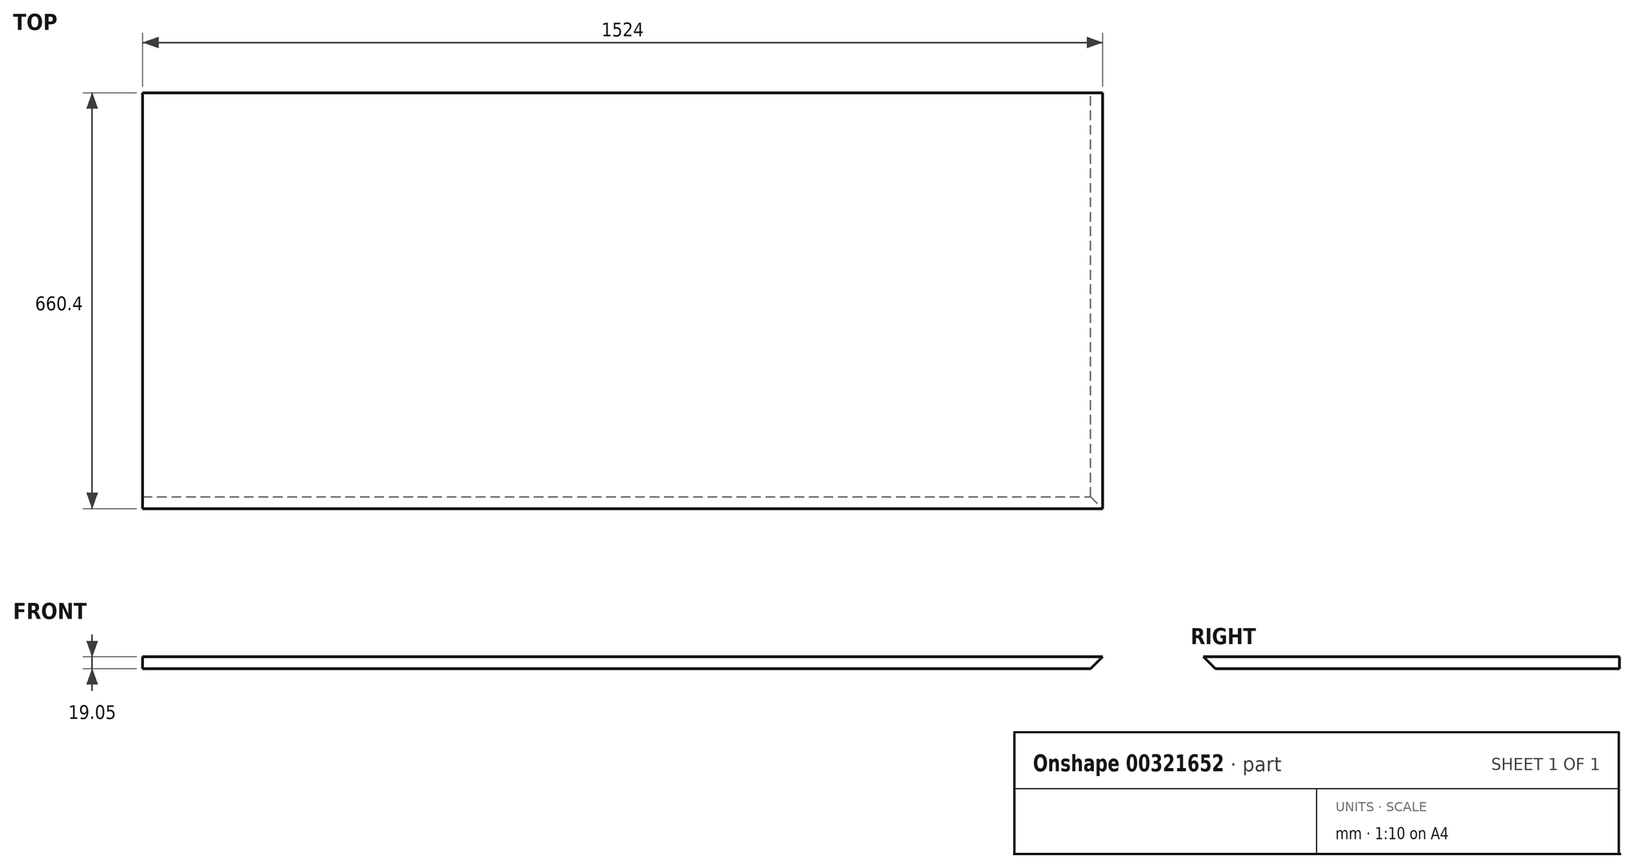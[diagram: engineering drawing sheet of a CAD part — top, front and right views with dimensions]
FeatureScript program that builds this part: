
annotation { "Feature Type Name" : "Feature", "Feature Type Description" : "" }
export const myFeature = defineFeature(function(context is Context, id is Id, definition is map)
    precondition{}
    {
        {
            var Q0;
            Q0=qCreatedBy(makeId("Top.planeOp"),FACE);
            var sketch = newSketch(context, id + "F0", { "sketchPlane" : qUnion([Q0])});
            skLineSegment(sketch, "E0.bottom", {"start": v(762, 330.2) * mm, "end": v(-762, 330.2) * mm});
            skLineSegment(sketch, "E0.top", {"start": v(762, -330.2) * mm, "end": v(-762, -330.2) * mm});
            skLineSegment(sketch, "E0.left", {"start": v(762, 330.2) * mm, "end": v(762, -330.2) * mm});
            skLineSegment(sketch, "E0.right", {"start": v(-762, 330.2) * mm, "end": v(-762, -330.2) * mm});
            skPoint(sketch, "E0.middle", {"position": v(0, 0) * mm});
            skSolve(sketch);
        }
        {
            var Q0;
            Q0=makeQuery(id+"F0.imprint","IMPRINT",FACE,{"disambiguationData":[TD([[makeQuery(id+"F0.imprint","IMPRINT",EDGE,{"derivedFrom":sQuery(id+"F0.wireOp",EDGE,"E0.bottom")}),1.0]])]});
            extrude(context, id + "F1", {"entities" : qUnion([Q0]), "depth" : 19.05 * mm});
        }
        {
            var Q0;
            Q0=makeQuery(id+"F1.opExtrude","SWEPT_FACE",FACE,{"disambiguationData":[OSD([sQuery(id+"F0.wireOp",EDGE,"E0.left")])]});
            var sketch = newSketch(context, id + "F2", { "sketchPlane" : qUnion([Q0])});
            skLineSegment(sketch, "E1", {"start": v(-330.2, 19.05) * mm, "end": v(-311.15, 0) * mm});
            skLineSegment(sketch, "E2", {"start": v(-311.15, 0) * mm, "end": v(-330.2, 0) * mm});
            skLineSegment(sketch, "E3", {"start": v(-330.2, 0) * mm, "end": v(-330.2, 19.05) * mm});
            skSolve(sketch);
        }
        {
            var Q0;
            Q0=makeQuery(id+"F2.imprint","IMPRINT",FACE,{"disambiguationData":[TD([[makeQuery(id+"F2.imprint","IMPRINT",EDGE,{"derivedFrom":sQuery(id+"F2.wireOp",EDGE,"E1")}),-1.0]])]});
            extrude(context, id + "F3", {"entities" : qUnion([Q0]), "operationType" : NewBodyOperationType.REMOVE, "endBound" : BoundingType.THROUGH_ALL, "oppositeDirection" : true, "depth" : 25.4 * mm});
        }
        {
            var Q0;
            Q0=makeQuery(id+"F1.opExtrude","SWEPT_FACE",FACE,{"disambiguationData":[OSD([sQuery(id+"F0.wireOp",EDGE,"E0.bottom")])]});
            var sketch = newSketch(context, id + "F4", { "sketchPlane" : qUnion([Q0])});
            skLineSegment(sketch, "E4", {"start": v(-762, 19.05) * mm, "end": v(-742.95, 0) * mm});
            skLineSegment(sketch, "E5", {"start": v(-742.95, 0) * mm, "end": v(-762, 0) * mm});
            skLineSegment(sketch, "E6", {"start": v(-762, 0) * mm, "end": v(-762, 19.05) * mm});
            skSolve(sketch);
        }
        {
            var Q0;
            Q0=makeQuery(id+"F4.imprint","IMPRINT",FACE,{"disambiguationData":[TD([[makeQuery(id+"F4.imprint","IMPRINT",EDGE,{"derivedFrom":sQuery(id+"F4.wireOp",EDGE,"E4")}),-1.0]])]});
            extrude(context, id + "F5", {"entities" : qUnion([Q0]), "operationType" : NewBodyOperationType.REMOVE, "endBound" : BoundingType.THROUGH_ALL, "oppositeDirection" : true, "depth" : 25.4 * mm});
        }
    });
